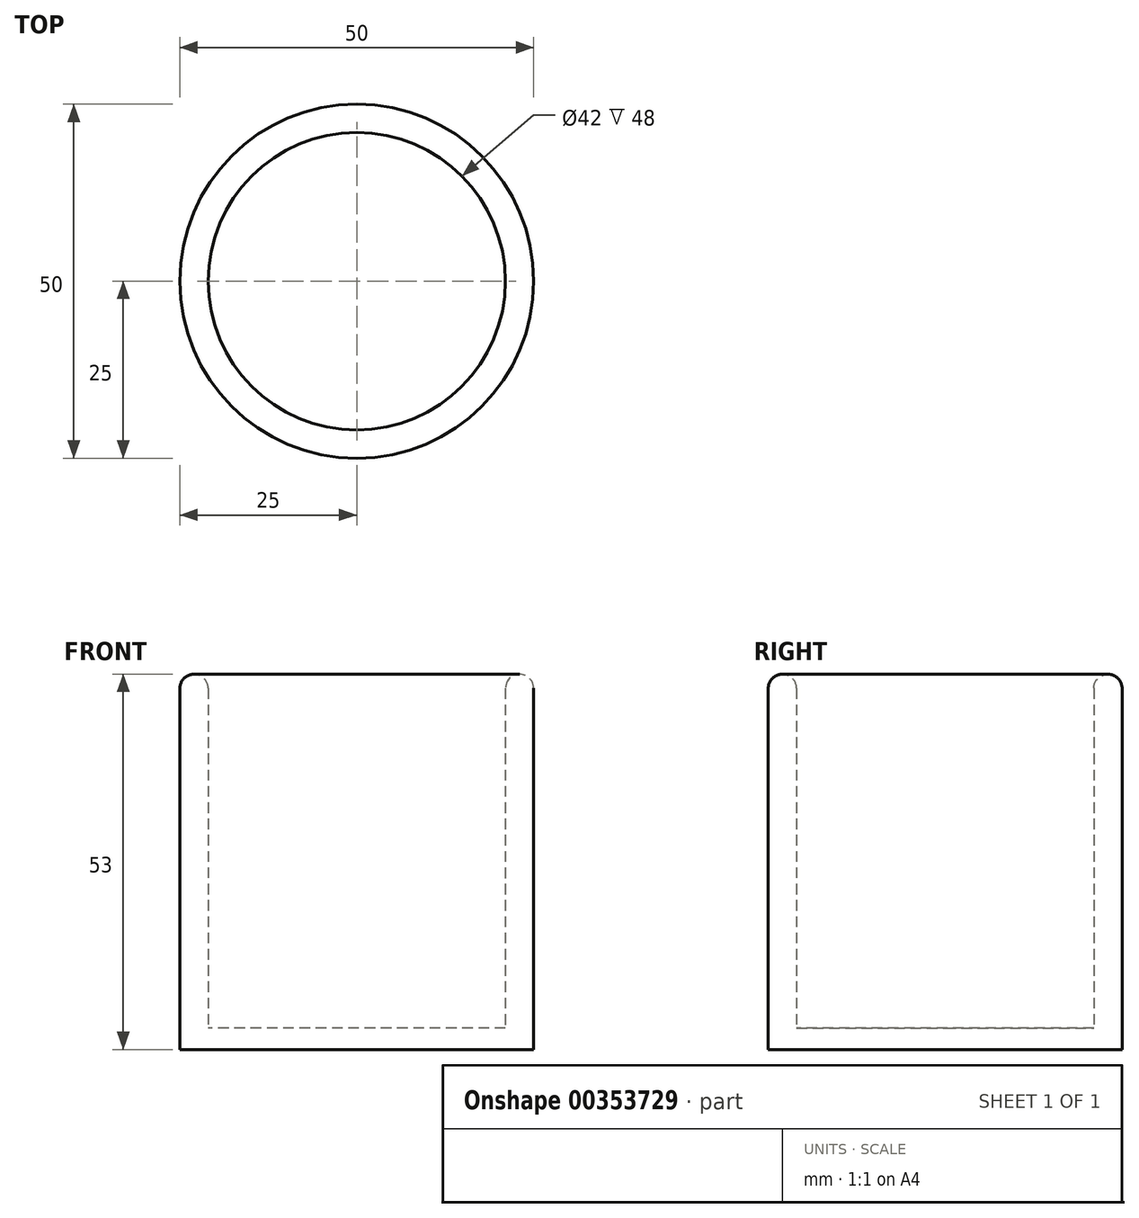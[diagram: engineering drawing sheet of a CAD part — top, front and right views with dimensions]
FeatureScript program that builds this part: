
annotation { "Feature Type Name" : "Feature", "Feature Type Description" : "" }
export const myFeature = defineFeature(function(context is Context, id is Id, definition is map)
    precondition{}
    {
        {
            var Q0;
            Q0=qCreatedBy(makeId("Top.planeOp"),FACE);
            var sketch = newSketch(context, id + "F0", { "sketchPlane" : qUnion([Q0])});
            skCircle(sketch, "E0", {"center": v(0, 0) * mm, "radius": 25 * mm});
            skSolve(sketch);
        }
        {
            var Q0;
            Q0 = qSketchRegion(id + "F0", true);
            extrude(context, id + "F1", {"entities" : qUnion([Q0]), "depth" : 3 * mm});
        }
        {
            var Q0;
            Q0=makeQuery(id+"F1.opExtrude","CAP_FACE",FACE,{"disambiguationData":[OSD([sQuery(id+"F0.wireOp",EDGE,"E0")])],"isStart":false});
            var sketch = newSketch(context, id + "F2", { "sketchPlane" : qUnion([Q0])});
            skCircle(sketch, "E1", {"center": v(0, 0) * mm, "radius": 21 * mm});
            skSolve(sketch);
        }
        {
            var Q0;
            Q0=makeQuery(id+"F2.imprint","IMPRINT",FACE,{"disambiguationData":[TD([[makeQuery(id+"F2.imprint","IMPRINT",EDGE,{"derivedFrom":sQuery(id+"F2.wireOp",EDGE,"E1")}),-1.0]])]});
            extrude(context, id + "F3", {"entities" : qUnion([Q0]), "operationType" : NewBodyOperationType.ADD, "depth" : 50 * mm});
        }
        {
            var Q0;
            Q0=makeQuery(id+"F3.opExtrude","CAP_EDGE",EDGE,{"disambiguationData":[OSD([sQuery(id+"F0.wireOp",EDGE,"E0")])],"isStart":false});
            var Q1;
            Q1=makeQuery(id+"F3.opExtrude","CAP_EDGE",EDGE,{"disambiguationData":[OSD([sQuery(id+"F2.wireOp",EDGE,"E1")])],"isStart":false});
            fillet(context, id + "F4", {"entities" : qUnion([Q0, Q1]), "radius" : 2 * mm, "tangentPropagation" : true, "allowEdgeOverflow" : false});
        }
    });
